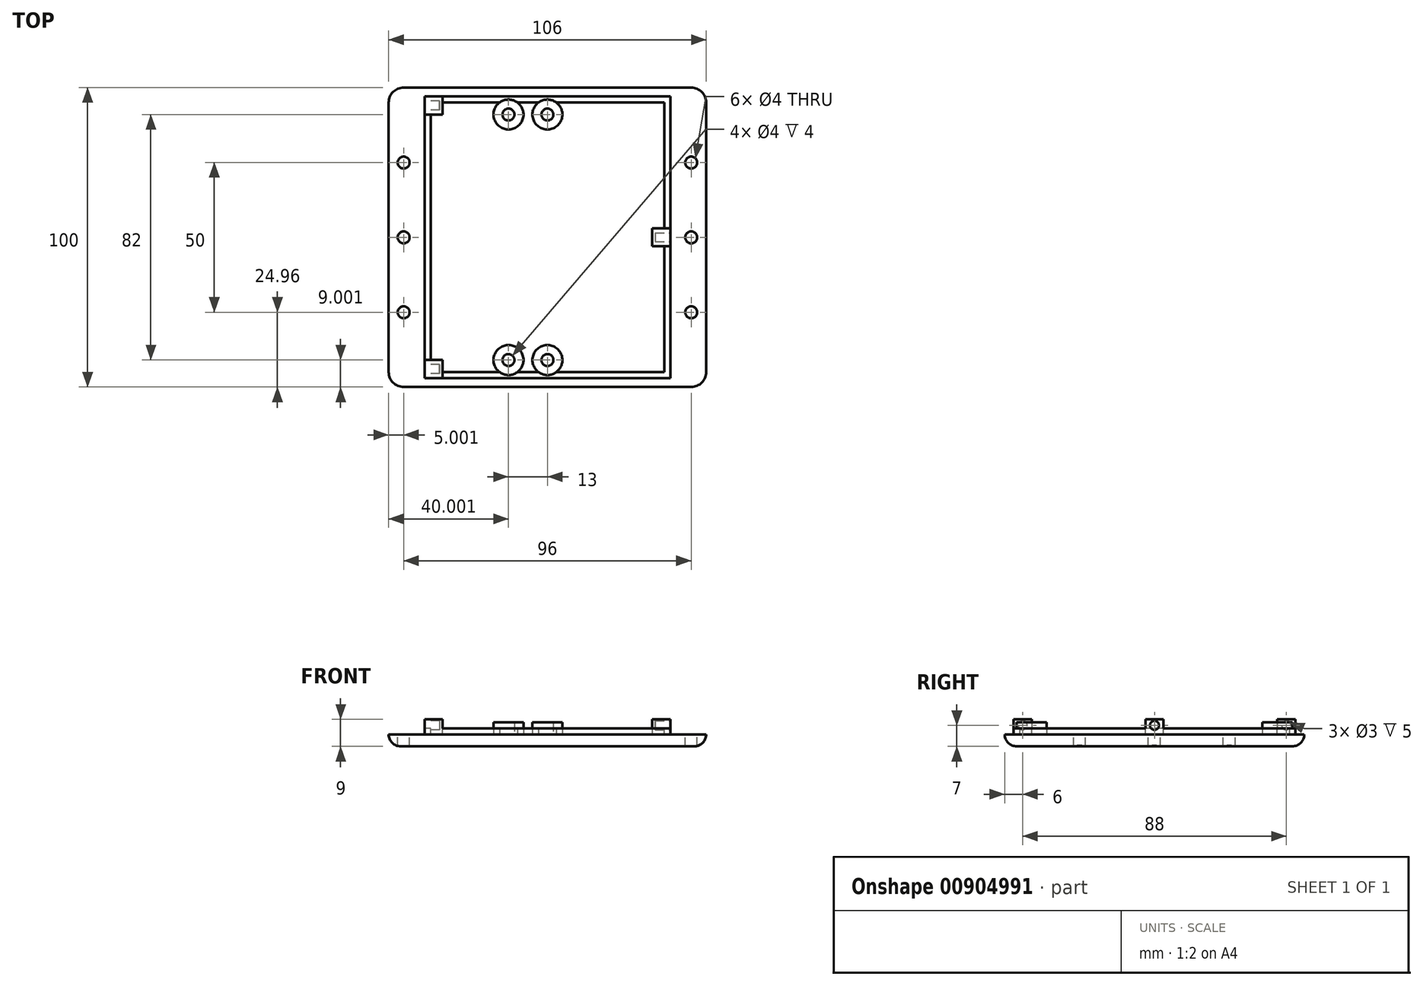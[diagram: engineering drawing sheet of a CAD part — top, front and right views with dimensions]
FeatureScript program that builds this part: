
annotation { "Feature Type Name" : "Feature", "Feature Type Description" : "" }
export const myFeature = defineFeature(function(context is Context, id is Id, definition is map)
    precondition{}
    {
        {
            var Q0;
            Q0=qCreatedBy(makeId("Top.planeOp"),FACE);
            var sketch = newSketch(context, id + "F0", { "sketchPlane" : qUnion([Q0])});
            skLineSegment(sketch, "E0.bottom", {"start": v(-82.94, 76.84) * mm, "end": v(23.06, 76.84) * mm});
            skLineSegment(sketch, "E0.top", {"start": v(-82.94, -23.16) * mm, "end": v(23.06, -23.16) * mm});
            skLineSegment(sketch, "E0.left", {"start": v(-82.94, 76.84) * mm, "end": v(-82.94, -23.16) * mm});
            skLineSegment(sketch, "E0.right", {"start": v(23.06, 76.84) * mm, "end": v(23.06, -23.16) * mm});
            skSolve(sketch);
        }
        {
            var Q0;
            Q0=makeQuery(id+"F0.imprint","IMPRINT",FACE,{"disambiguationData":[TD([[makeQuery(id+"F0.imprint","IMPRINT",EDGE,{"derivedFrom":sQuery(id+"F0.wireOp",EDGE,"E0.bottom")}),-1.0]])]});
            extrude(context, id + "F1", {"entities" : qUnion([Q0]), "depth" : 4 * mm, "offsetDistance" : 25 * mm});
        }
        {
            var Q0;
            Q0=makeQuery(id+"F1.opExtrude","CAP_FACE",FACE,{"disambiguationData":[OSD([sQuery(id+"F0.wireOp",EDGE,"E0.bottom"),sQuery(id+"F0.wireOp",EDGE,"E0.top"),sQuery(id+"F0.wireOp",EDGE,"E0.left"),sQuery(id+"F0.wireOp",EDGE,"E0.right")])],"isStart":false});
            var sketch = newSketch(context, id + "F2", { "sketchPlane" : qUnion([Q0])});
            skLineSegment(sketch, "E1.bottom", {"start": v(-70.94, 73.84) * mm, "end": v(11.06, 73.84) * mm});
            skLineSegment(sketch, "E1.top", {"start": v(-70.94, -20.16) * mm, "end": v(11.06, -20.16) * mm});
            skLineSegment(sketch, "E1.left", {"start": v(-70.94, 73.84) * mm, "end": v(-70.94, -20.16) * mm});
            skLineSegment(sketch, "E1.right", {"start": v(11.06, 73.84) * mm, "end": v(11.06, -20.16) * mm});
            skLineSegment(sketch, "E2.bottom", {"start": v(-68.94, 71.84) * mm, "end": v(9.06, 71.84) * mm});
            skLineSegment(sketch, "E2.top", {"start": v(-68.94, -18.16) * mm, "end": v(9.06, -18.16) * mm});
            skLineSegment(sketch, "E2.left", {"start": v(-68.94, 71.84) * mm, "end": v(-68.94, -18.16) * mm});
            skLineSegment(sketch, "E2.right", {"start": v(9.06, 71.84) * mm, "end": v(9.06, -18.16) * mm});
            skSolve(sketch);
        }
        {
            var Q0;
            Q0=makeQuery(id+"F2.imprint","IMPRINT",FACE,{"disambiguationData":[TD([[makeQuery(id+"F2.imprint","IMPRINT",EDGE,{"derivedFrom":sQuery(id+"F2.wireOp",EDGE,"E1.bottom")}),1.0]])]});
            var sketch = newSketch(context, id + "F3", { "sketchPlane" : qUnion([Q0])});
            skCircle(sketch, "E3", {"center": v(-77.94, 51.8) * mm, "radius": 2 * mm});
            skCircle(sketch, "E4", {"center": v(-77.94, 26.8) * mm, "radius": 2 * mm});
            skCircle(sketch, "E5", {"center": v(-77.94, 1.8) * mm, "radius": 2 * mm});
            skLineSegment(sketch, "E6", {"start": v(-77.94, 51.8) * mm, "end": v(-77.94, 26.8) * mm});
            skLineSegment(sketch, "E7", {"start": v(-77.94, 26.8) * mm, "end": v(-77.94, 1.8) * mm});
            skLineSegment(sketch, "E8", {"start": v(-77.94, 51.8) * mm, "end": v(-77.94, 76.8) * mm});
            skLineSegment(sketch, "E9", {"start": v(-77.94, 1.8) * mm, "end": v(-77.94, -23.2) * mm});
            skCircle(sketch, "E10", {"center": v(18.06, 51.8) * mm, "radius": 2 * mm});
            skCircle(sketch, "E11", {"center": v(18.06, 26.8) * mm, "radius": 2 * mm});
            skLineSegment(sketch, "E12", {"start": v(18.06, 51.8) * mm, "end": v(18.06, 26.8) * mm});
            skLineSegment(sketch, "E13", {"start": v(18.06, 26.8) * mm, "end": v(18.06, 1.8) * mm});
            skLineSegment(sketch, "E14", {"start": v(18.06, 51.8) * mm, "end": v(18.06, 76.8) * mm});
            skLineSegment(sketch, "E15", {"start": v(12.02, 1.8) * mm, "end": v(12.02, -23.2) * mm});
            skCircle(sketch, "E16", {"center": v(18.06, 1.8) * mm, "radius": 2 * mm});
            skSolve(sketch);
        }
        {
            var Q0;
            Q0=makeQuery(id+"F2.imprint","IMPRINT",FACE,{"disambiguationData":[TD([[makeQuery(id+"F2.imprint","IMPRINT",EDGE,{"derivedFrom":sQuery(id+"F2.wireOp",EDGE,"E1.bottom")}),1.0]])]});
            var sketch = newSketch(context, id + "F4", { "sketchPlane" : qUnion([Q0])});
            skCircle(sketch, "E17", {"center": v(-42.94, 67.84) * mm, "radius": 2 * mm});
            skCircle(sketch, "E18", {"center": v(-42.94, 67.84) * mm, "radius": 5 * mm});
            skCircle(sketch, "E19", {"center": v(-29.94, 67.84) * mm, "radius": 2 * mm});
            skCircle(sketch, "E20", {"center": v(-29.94, 67.84) * mm, "radius": 5 * mm});
            skCircle(sketch, "E21", {"center": v(-42.94, -14.16) * mm, "radius": 2 * mm});
            skCircle(sketch, "E22", {"center": v(-42.94, -14.16) * mm, "radius": 5 * mm});
            skCircle(sketch, "E23", {"center": v(-29.94, -14.16) * mm, "radius": 2 * mm});
            skCircle(sketch, "E24", {"center": v(-29.94, -14.16) * mm, "radius": 5 * mm});
            skSolve(sketch);
        }
        {
            var Q0;
            Q0 = qSketchRegion(id + "F2", true);
            extrude(context, id + "F5", {"entities" : qUnion([Q0]), "operationType" : NewBodyOperationType.ADD, "depth" : 2 * mm, "offsetDistance" : 25 * mm});
        }
        {
            var Q0;
            Q0 = qSketchRegion(id + "F3", true);
            extrude(context, id + "F6", {"entities" : qUnion([Q0]), "operationType" : NewBodyOperationType.REMOVE, "oppositeDirection" : true, "depth" : 25 * mm, "offsetDistance" : 25 * mm});
        }
        {
            var Q0;
            Q0 = qSketchRegion(id + "F4", true);
            extrude(context, id + "F7", {"entities" : qUnion([Q0]), "operationType" : NewBodyOperationType.ADD, "depth" : 4 * mm, "offsetDistance" : 25 * mm});
        }
        {
            var Q0;
            Q0=makeQuery(id+"F2.imprint","IMPRINT",FACE,{"disambiguationData":[TD([[makeQuery(id+"F2.imprint","IMPRINT",EDGE,{"derivedFrom":sQuery(id+"F2.wireOp",EDGE,"E1.bottom")}),1.0]])]});
            var sketch = newSketch(context, id + "F8", { "sketchPlane" : qUnion([Q0])});
            skLineSegment(sketch, "E25.bottom", {"start": v(-70.94, 73.84) * mm, "end": v(-64.94, 73.84) * mm});
            skLineSegment(sketch, "E25.top", {"start": v(-70.94, 67.84) * mm, "end": v(-64.94, 67.84) * mm});
            skLineSegment(sketch, "E25.left", {"start": v(-70.94, 73.84) * mm, "end": v(-70.94, 67.84) * mm});
            skLineSegment(sketch, "E25.right", {"start": v(-64.94, 73.84) * mm, "end": v(-64.94, 67.84) * mm});
            skLineSegment(sketch, "E26.bottom", {"start": v(-70.94, -20.16) * mm, "end": v(-64.94, -20.16) * mm});
            skLineSegment(sketch, "E26.top", {"start": v(-70.94, -14.16) * mm, "end": v(-64.94, -14.16) * mm});
            skLineSegment(sketch, "E26.left", {"start": v(-70.94, -20.16) * mm, "end": v(-70.94, -14.16) * mm});
            skLineSegment(sketch, "E26.right", {"start": v(-64.94, -20.16) * mm, "end": v(-64.94, -14.16) * mm});
            skSolve(sketch);
        }
        {
            var Q0;
            Q0 = qSketchRegion(id + "F8", true);
            extrude(context, id + "F9", {"entities" : qUnion([Q0]), "operationType" : NewBodyOperationType.ADD, "depth" : 5 * mm, "offsetDistance" : 25 * mm});
        }
        {
            var Q0;
            Q0=makeQuery(id+"F9.boolean.opBoolean","MERGE",FACE,{"derivedFrom":[makeQuery(id+"F5.opExtrude","SWEPT_FACE",FACE,{"disambiguationData":[OSD([sQuery(id+"F2.wireOp",EDGE,"E1.left")])]}),makeQuery(id+"F9.opExtrude","SWEPT_FACE",FACE,{"disambiguationData":[OSD([sQuery(id+"F8.wireOp",EDGE,"E25.left")])]}),makeQuery(id+"F9.opExtrude","SWEPT_FACE",FACE,{"disambiguationData":[OSD([sQuery(id+"F8.wireOp",EDGE,"E26.left")])]})]});
            var sketch = newSketch(context, id + "F10", { "sketchPlane" : qUnion([Q0])});
            skCircle(sketch, "E27", {"center": v(-70.84, 7) * mm, "radius": 1.5 * mm});
            skCircle(sketch, "E28", {"center": v(17.16, 7) * mm, "radius": 1.5 * mm});
            skSolve(sketch);
        }
        {
            var Q0;
            Q0 = qSketchRegion(id + "F10", true);
            extrude(context, id + "F11", {"entities" : qUnion([Q0]), "operationType" : NewBodyOperationType.REMOVE, "oppositeDirection" : true, "depth" : 5 * mm, "offsetDistance" : 25 * mm});
        }
        {
            var Q0;
            Q0=makeQuery(id+"F2.imprint","IMPRINT",FACE,{"disambiguationData":[TD([[makeQuery(id+"F2.imprint","IMPRINT",EDGE,{"derivedFrom":sQuery(id+"F2.wireOp",EDGE,"E2.bottom")}),-1.0]])]});
            var sketch = newSketch(context, id + "F12", { "sketchPlane" : qUnion([Q0])});
            skLineSegment(sketch, "E29.bottom", {"start": v(5.06, 23.84) * mm, "end": v(11.06, 23.84) * mm});
            skLineSegment(sketch, "E29.top", {"start": v(5.06, 29.84) * mm, "end": v(11.06, 29.84) * mm});
            skLineSegment(sketch, "E29.left", {"start": v(5.06, 23.84) * mm, "end": v(5.06, 29.84) * mm});
            skLineSegment(sketch, "E29.right", {"start": v(11.06, 23.84) * mm, "end": v(11.06, 29.84) * mm});
            skPoint(sketch, "E30.startSnap0", {"position": v(11.06, 26.84) * mm});
            skSolve(sketch);
        }
        {
            var Q0;
            Q0 = qSketchRegion(id + "F12", true);
            extrude(context, id + "F13", {"entities" : qUnion([Q0]), "operationType" : NewBodyOperationType.ADD, "depth" : 5 * mm, "offsetDistance" : 25 * mm});
        }
        {
            var Q0;
            Q0=makeQuery(id+"F13.boolean.opBoolean","MERGE",FACE,{"derivedFrom":[makeQuery(id+"F5.opExtrude","SWEPT_FACE",FACE,{"disambiguationData":[OSD([sQuery(id+"F2.wireOp",EDGE,"E1.right")])]}),makeQuery(id+"F13.opExtrude","SWEPT_FACE",FACE,{"disambiguationData":[OSD([sQuery(id+"F12.wireOp",EDGE,"E29.right")])]})]});
            var sketch = newSketch(context, id + "F14", { "sketchPlane" : qUnion([Q0])});
            skCircle(sketch, "E31", {"center": v(26.84, 7) * mm, "radius": 1.5 * mm});
            skSolve(sketch);
        }
        {
            var Q0;
            Q0 = qSketchRegion(id + "F14", true);
            extrude(context, id + "F15", {"entities" : qUnion([Q0]), "operationType" : NewBodyOperationType.REMOVE, "oppositeDirection" : true, "depth" : 5 * mm, "offsetDistance" : 25 * mm});
        }
        {
            var Q0;
            Q0=makeQuery(id+"F1.opExtrude","SWEPT_EDGE",EDGE,{"disambiguationData":[OSD([sQuery(id+"F0.wireOp",EDGE,"E0.bottom"),sQuery(id+"F0.wireOp",EDGE,"E0.left")])]});
            var Q1;
            Q1=makeQuery(id+"F1.opExtrude","SWEPT_EDGE",EDGE,{"disambiguationData":[OSD([sQuery(id+"F0.wireOp",EDGE,"E0.bottom"),sQuery(id+"F0.wireOp",EDGE,"E0.right")])]});
            var Q2;
            Q2=makeQuery(id+"F1.opExtrude","SWEPT_EDGE",EDGE,{"disambiguationData":[OSD([sQuery(id+"F0.wireOp",EDGE,"E0.top"),sQuery(id+"F0.wireOp",EDGE,"E0.right")])]});
            var Q3;
            Q3=makeQuery(id+"F1.opExtrude","SWEPT_EDGE",EDGE,{"disambiguationData":[OSD([sQuery(id+"F0.wireOp",EDGE,"E0.top"),sQuery(id+"F0.wireOp",EDGE,"E0.left")])]});
            fillet(context, id + "F16", {"entities" : qUnion([Q0, Q1, Q2, Q3]), "radius" : 5 * mm, "tangentPropagation" : true, "allowEdgeOverflow" : false});
        }
        {
            var Q0;
            Q0=makeQuery(id+"F1.opExtrude","CAP_EDGE",EDGE,{"disambiguationData":[OSD([sQuery(id+"F0.wireOp",EDGE,"E0.right")])],"isStart":true});
            fillet(context, id + "F17", {"entities" : qUnion([Q0]), "radius" : 4 * mm, "tangentPropagation" : true, "allowEdgeOverflow" : false});
        }
    });
